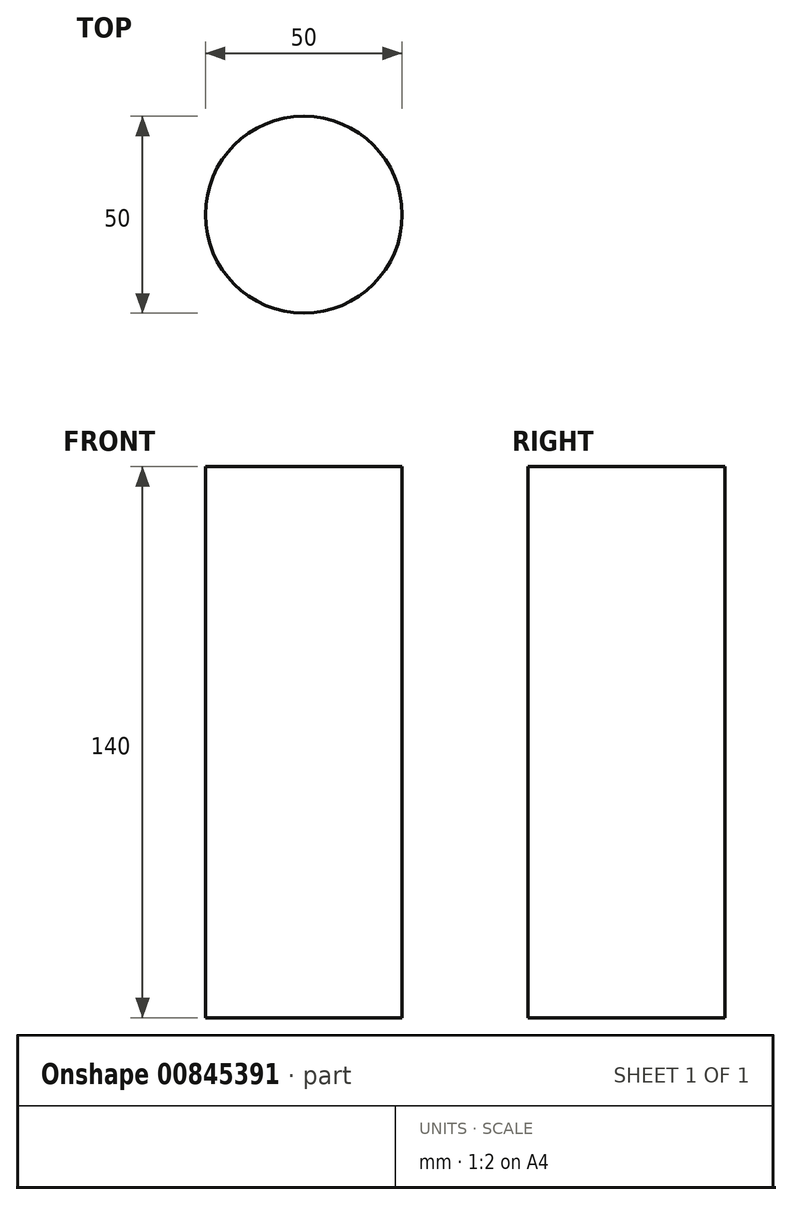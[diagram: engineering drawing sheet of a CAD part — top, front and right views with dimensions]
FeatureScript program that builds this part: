
annotation { "Feature Type Name" : "Feature", "Feature Type Description" : "" }
export const myFeature = defineFeature(function(context is Context, id is Id, definition is map)
    precondition{}
    {
        {
            var Q0;
            Q0=qCreatedBy(makeId("Top.planeOp"),FACE);
            var sketch = newSketch(context, id + "F0", { "sketchPlane" : qUnion([Q0])});
            skCircle(sketch, "E0", {"center": v(0, 0) * mm, "radius": 25 * mm});
            skSolve(sketch);
        }
        {
            var Q0;
            Q0=makeQuery(id+"F0.imprint","IMPRINT",FACE,{"disambiguationData":[TD([[makeQuery(id+"F0.imprint","IMPRINT",EDGE,{"derivedFrom":sQuery(id+"F0.wireOp",EDGE,"E0")}),1.0]])]});
            extrude(context, id + "F1", {"entities" : qUnion([Q0]), "depth" : 140 * mm, "offsetDistance" : 25 * mm});
        }
    });
